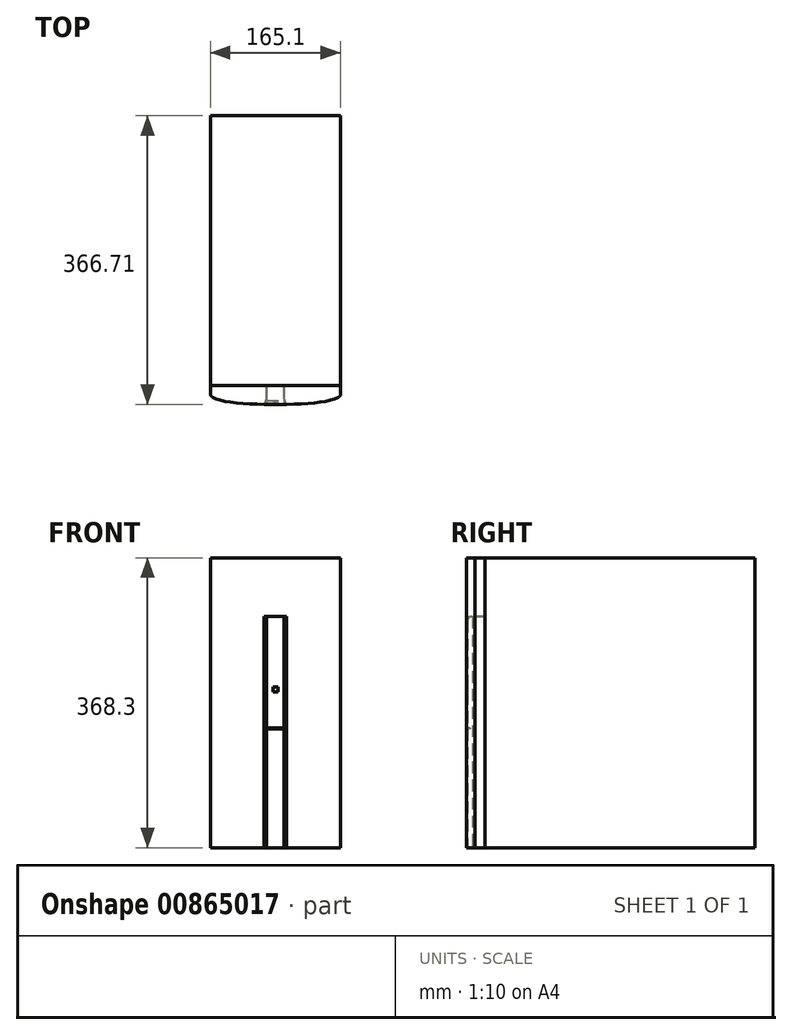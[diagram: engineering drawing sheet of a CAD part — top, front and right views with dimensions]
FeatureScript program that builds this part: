
annotation { "Feature Type Name" : "Feature", "Feature Type Description" : "" }
export const myFeature = defineFeature(function(context is Context, id is Id, definition is map)
    precondition{}
    {
        {
            var Q0;
            Q0=qCreatedBy(makeId("Top.planeOp"),FACE);
            var sketch = newSketch(context, id + "F0", { "sketchPlane" : qUnion([Q0])});
            skLineSegment(sketch, "E0.bottom", {"start": v(82.55, 171.45) * mm, "end": v(-82.55, 171.45) * mm});
            skLineSegment(sketch, "E0.top", {"start": v(82.55, -171.45) * mm, "end": v(-82.55, -171.45) * mm});
            skLineSegment(sketch, "E0.left", {"start": v(82.55, 171.45) * mm, "end": v(82.55, -171.45) * mm});
            skLineSegment(sketch, "E0.right", {"start": v(-82.55, 171.45) * mm, "end": v(-82.55, -171.45) * mm});
            skPoint(sketch, "E0.middle", {"position": v(0, 0) * mm});
            skSolve(sketch);
        }
        {
            var Q0;
            Q0 = qSketchRegion(id + "F0", true);
            extrude(context, id + "F1", {"entities" : qUnion([Q0]), "depth" : 368.3 * mm, "offsetDistance" : 25.4 * mm});
        }
        {
            var Q0;
            Q0=qCreatedBy(makeId("Top.planeOp"),FACE);
            var sketch = newSketch(context, id + "F2", { "sketchPlane" : qUnion([Q0])});
            skLineSegment(sketch, "E1.bottom", {"start": v(-82.55, -171.45) * mm, "end": v(82.55, -171.45) * mm});
            skLineSegment(sketch, "E1.top", {"start": v(-82.55, -184.15) * mm, "end": v(82.55, -184.15) * mm});
            skLineSegment(sketch, "E1.left", {"start": v(-82.55, -171.45) * mm, "end": v(-82.55, -184.15) * mm});
            skLineSegment(sketch, "E1.right", {"start": v(82.55, -171.45) * mm, "end": v(82.55, -184.15) * mm});
            skFitSpline(sketch, "E2", {"points": [v(-82.55, -184.15) * mm, v(0, -195.26) * mm, v(82.55, -184.15) * mm], "startDerivative": vector(57.86, -55.82) * mm, "endDerivative": vector(57.86, 55.82) * mm});
            skSolve(sketch);
        }
        {
            var Q0;
            Q0 = qSketchRegion(id + "F2", true);
            var Q1;
            Q1=makeQuery(id+"F1.opExtrude","CAP_FACE",FACE,{"disambiguationData":[OSD([sQuery(id+"F0.wireOp",EDGE,"E0.bottom"),sQuery(id+"F0.wireOp",EDGE,"E0.top"),sQuery(id+"F0.wireOp",EDGE,"E0.left"),sQuery(id+"F0.wireOp",EDGE,"E0.right")])],"isStart":false});
            extrude(context, id + "F3", {"entities" : qUnion([Q0]), "endBound" : BoundingType.UP_TO_SURFACE, "depth" : 312.42 * mm, "endBoundEntityFace" : qUnion([Q1]), "offsetDistance" : 25.4 * mm});
        }
        {
            var Q0;
            Q0=makeQuery(id+"F3.opExtrude","CAP_FACE",FACE,{"disambiguationData":[OSD([sQuery(id+"F2.wireOp",EDGE,"E1.bottom"),sQuery(id+"F2.wireOp",EDGE,"E1.left"),sQuery(id+"F2.wireOp",EDGE,"E1.right"),sQuery(id+"F2.wireOp",EDGE,"E2")])],"isStart":true});
            var sketch = newSketch(context, id + "F4", { "sketchPlane" : qUnion([Q0])});
            skLineSegment(sketch, "E3", {"start": v(-14.29, 195.16) * mm, "end": v(14.29, 195.16) * mm, "construction": true});
            skLineSegment(sketch, "E4.bottom", {"start": v(-11.11, 171.45) * mm, "end": v(11.11, 171.45) * mm});
            skLineSegment(sketch, "E4.top", {"start": v(-11.11, 187.33) * mm, "end": v(11.11, 187.33) * mm});
            skLineSegment(sketch, "E4.left", {"start": v(-11.11, 171.45) * mm, "end": v(-11.11, 187.33) * mm});
            skLineSegment(sketch, "E4.right", {"start": v(11.11, 171.45) * mm, "end": v(11.11, 187.33) * mm});
            skLineSegment(sketch, "E5", {"start": v(-11.11, 187.33) * mm, "end": v(-14.33, 195.26) * mm});
            skLineSegment(sketch, "E6", {"start": v(-14.33, 195.26) * mm, "end": v(14.33, 195.26) * mm});
            skLineSegment(sketch, "E7", {"start": v(14.33, 195.26) * mm, "end": v(11.11, 187.33) * mm});
            skSolve(sketch);
        }
        {
            var Q0;
            Q0 = qSketchRegion(id + "F4", true);
            extrude(context, id + "F5", {"entities" : qUnion([Q0]), "operationType" : NewBodyOperationType.REMOVE, "oppositeDirection" : true, "depth" : 293.7 * mm, "offsetDistance" : 25.4 * mm});
        }
        {
            var Q0;
            {var subQ0=sQuery(id+"F2.wireOp",EDGE,"E2");var subQ1=sQuery(id+"F2.wireOp",EDGE,"E1.right");var subQ2=sQuery(id+"F2.wireOp",EDGE,"E1.bottom");Q0=makeQuery(id+"F5.boolean.opBoolean","SPLIT",FACE,{"disambiguationData":[TD([makeQuery(id+"F3.opExtrude","SWEPT_FACE",FACE,{"disambiguationData":[OSD([subQ1])]})])],"derivedFrom":makeQuery(id+"F3.opExtrude","CAP_FACE",FACE,{"disambiguationData":[OSD([subQ2,sQuery(id+"F2.wireOp",EDGE,"E1.left"),subQ1,subQ0])],"isStart":true})});}
            var sketch = newSketch(context, id + "F6", { "sketchPlane" : qUnion([Q0])});
            skLineSegment(sketch, "E8.bottom", {"start": v(-11.11, 171.45) * mm, "end": v(11.11, 171.45) * mm});
            skLineSegment(sketch, "E8.top", {"start": v(-11.11, 193.68) * mm, "end": v(11.11, 193.68) * mm});
            skLineSegment(sketch, "E8.left", {"start": v(-11.11, 171.45) * mm, "end": v(-11.11, 193.68) * mm});
            skLineSegment(sketch, "E8.right", {"start": v(11.11, 171.45) * mm, "end": v(11.11, 193.68) * mm});
            skPoint(sketch, "E9.visualSharp", {"position": v(-11.11, 193.68) * mm});
            skPoint(sketch, "E10.visualSharp", {"position": v(11.11, 193.68) * mm});
            skSolve(sketch);
        }
        {
            var Q0;
            {var subQ1=sQuery(id+"F6.wireOp",EDGE,"E8.bottom");Q0=makeQuery(id+"F6.imprint","IMPRINT",FACE,{"disambiguationData":[TD([[makeQuery(id+"F6.imprint","IMPRINT",EDGE,{"derivedFrom":subQ1}),1.0]])]});}
            var Q1;
            Q1=makeQuery(id+"F5.boolean.opBoolean","COPY",FACE,{"derivedFrom":makeQuery(id+"F5.opExtrude","CAP_FACE",FACE,{"disambiguationData":[OSD([sQuery(id+"F4.wireOp",EDGE,"E4.bottom"),sQuery(id+"F4.wireOp",EDGE,"E4.left"),sQuery(id+"F4.wireOp",EDGE,"E4.right"),sQuery(id+"F4.wireOp",EDGE,"E5"),sQuery(id+"F4.wireOp",EDGE,"E6"),sQuery(id+"F4.wireOp",EDGE,"E7")])],"isStart":false})});
            extrude(context, id + "F7", {"entities" : qUnion([Q0]), "endBound" : BoundingType.UP_TO_SURFACE, "oppositeDirection" : true, "depth" : 25.4 * mm, "endBoundEntityFace" : qUnion([Q1]), "offsetDistance" : 25.4 * mm});
        }
        {
            var Q0;
            Q0=makeQuery(id+"F7.opExtrude","CAP_EDGE",EDGE,{"disambiguationData":[OSD([sQuery(id+"F6.wireOp",EDGE,"E8.top")])],"isStart":false});
            fillet(context, id + "F8", {"entities" : qUnion([Q0]), "radius" : 5.08 * mm, "tangentPropagation" : true, "allowEdgeOverflow" : false});
        }
        {
            var Q0;
            Q0=makeQuery(id+"F7.opExtrude","SWEPT_FACE",FACE,{"disambiguationData":[OSD([sQuery(id+"F6.wireOp",EDGE,"E8.top")])]});
            var sketch = newSketch(context, id + "F9", { "sketchPlane" : qUnion([Q0])});
            skLineSegment(sketch, "E11.bottom", {"start": v(-11.11, 150.81) * mm, "end": v(11.11, 150.81) * mm});
            skLineSegment(sketch, "E11.top", {"start": v(-11.11, 152) * mm, "end": v(11.11, 152) * mm});
            skLineSegment(sketch, "E11.left", {"start": v(-11.11, 150.81) * mm, "end": v(-11.11, 152) * mm});
            skLineSegment(sketch, "E11.right", {"start": v(11.11, 150.81) * mm, "end": v(11.11, 152) * mm});
            skSolve(sketch);
        }
        {
            var Q0;
            Q0 = qSketchRegion(id + "F9", true);
            extrude(context, id + "F10", {"entities" : qUnion([Q0]), "operationType" : NewBodyOperationType.REMOVE, "oppositeDirection" : true, "depth" : 3.17 * mm, "offsetDistance" : 25.4 * mm});
        }
        {
            var Q0;
            {var subQ0=sQuery(id+"F6.wireOp",EDGE,"E8.top");Q0=makeQuery(id+"F10.boolean.opBoolean","SPLIT",FACE,{"disambiguationData":[TD([makeQuery(id+"F8.opFillet","BLEND_FACE",FACE,{"disambiguationData":[OSD([subQ0])]})])],"derivedFrom":makeQuery(id+"F7.opExtrude","SWEPT_FACE",FACE,{"disambiguationData":[OSD([subQ0])]})});}
            var sketch = newSketch(context, id + "F11", { "sketchPlane" : qUnion([Q0])});
            skLineSegment(sketch, "E12.bottom", {"start": v(3.17, 204.4) * mm, "end": v(-3.18, 204.4) * mm});
            skLineSegment(sketch, "E12.top", {"start": v(3.17, 198.04) * mm, "end": v(-3.18, 198.04) * mm});
            skLineSegment(sketch, "E12.left", {"start": v(3.17, 204.4) * mm, "end": v(3.17, 198.04) * mm});
            skLineSegment(sketch, "E12.right", {"start": v(-3.18, 204.4) * mm, "end": v(-3.18, 198.04) * mm});
            skPoint(sketch, "E12.middle", {"position": v(0, 201.22) * mm});
            skSolve(sketch);
        }
        {
            var Q0;
            Q0 = qSketchRegion(id + "F11", true);
            extrude(context, id + "F12", {"entities" : qUnion([Q0]), "operationType" : NewBodyOperationType.ADD, "depth" : 0.8 * mm, "offsetDistance" : 25.4 * mm});
        }
    });
